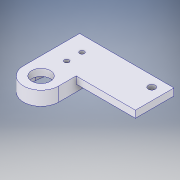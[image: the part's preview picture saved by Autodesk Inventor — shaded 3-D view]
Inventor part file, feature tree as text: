
AUTODESK INVENTOR PART (.ipt)
format: ipt  version: 2017 (Build 210142000, 142)  size: 164,352 bytes
history: native  units: in
note: dims shown in document units (in); Inventor stores cm internally (conversion verified against a paired STEP export)
features: extrude x3, sketch x3, projected_geometry x1
ambient origin geometry x8: Origin, YZ Plane, XZ Plane, XY Plane, X Axis, Y Axis, Z Axis, Center Point
bodies: Solid1 (feature_tree)
feature tree (7):
  extrude  "Extrusion1"  TaperAngle=90.0deg  [1 undecoded]
  extrude  "Extrusion3"  Depth=1.0in
  extrude  "Extrusion4"  Depth=0.5906in
  sketch  "Sketch3"  dims[d6=2.3622in d7=90.0deg]
  sketch  "Sketch6"  dims[d8=0.4929in d9=1.0in]
  projected_geometry  "Projected Loop3"
  sketch  "Sketch7"  dims[d10=0.2953in d11=0.5906in d13=0.9456in d14=0.1181in d15=0.0in d18=0.1969in d19=0.4724in d20=0.4724in d21=0.1181in d22=0.1181in d25=0.315in d26=0.4335in d27=0.2562in d28=0.0787in d29=0.0787in d31=0.4331in d32=0.0591in d33=0.2362in d34=0.1181in d35=0.2362in d36=0.0in d37=1.0in d38=0.0in]
note: 1 required parameter value undecoded (feature->parameter linkage not recoverable at this tier; creation-order binding heuristic only, values carry confidence <= 0.55)
